FCSTD DOCUMENT  (FreeCAD 0.21R33771 (Git))
Label: automation_t1
License: All rights reserved
LicenseURL: http://en.wikipedia.org/wiki/All_rights_reserved
objects: Sketcher::SketchObject×2, PartDesign::Body×2
note: 4 computed .brp shape members not serialized (recipe doc carries the construction recipe); baked Part::Feature solids carry a one-line shape summary decoded from their .brp

FEATURE [Sketcher::SketchObject] Sketch
  FullyConstrained = false
  MapMode = 5
  Support = -> [XY_Plane]
  sketch-geometry (4):
    g0: LineSegment StartX=-34.2131 StartY=10.468 StartZ=0 EndX=33.8221 EndY=10.468 EndZ=0
    g1: LineSegment StartX=33.8221 StartY=10.468 StartZ=0 EndX=33.8221 EndY=-11.532 EndZ=0
    g2: LineSegment StartX=33.8221 StartY=-11.532 StartZ=0 EndX=-34.2131 EndY=-11.532 EndZ=0
    g3: LineSegment StartX=-34.2131 StartY=-11.532 StartZ=0 EndX=-34.2131 EndY=10.468 EndZ=0
  constraints (10):
    c: Coincident(g0,g1)
    c: Coincident(g1,g2)
    c: Coincident(g2,g3)
    c: Coincident(g3,g0)
    c: Horizontal(g0)
    c: Horizontal(g2)
    c: Vertical(g1)
    c: Vertical(g3)
    c: DistanceX(g0,g0) = 68.0352  'lr1'
    c: DistanceY(g1,g1) = 22  'wr1'
FEATURE [PartDesign::Body] Body001
  Origin = -> Origin001
FEATURE [Sketcher::SketchObject] Sketch001
  FullyConstrained = true
FEATURE [PartDesign::Body] Body
  Group = -> [Sketch,Sketch001]
  Origin = -> Origin
